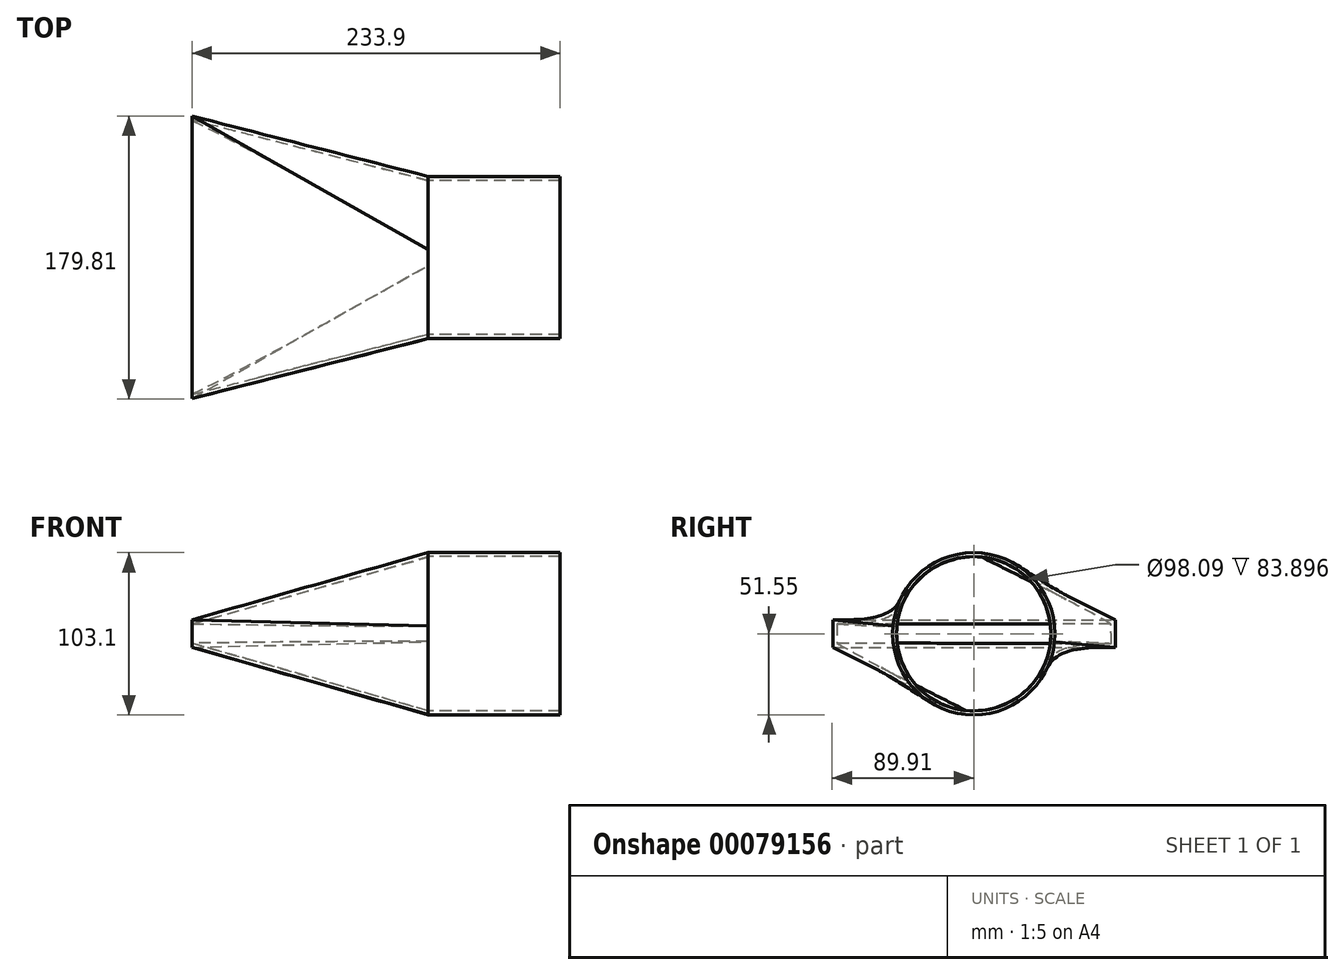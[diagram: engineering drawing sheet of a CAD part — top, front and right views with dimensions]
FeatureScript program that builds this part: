
annotation { "Feature Type Name" : "Feature", "Feature Type Description" : "" }
export const myFeature = defineFeature(function(context is Context, id is Id, definition is map)
    precondition{}
    {
        {
            var Q0;
            Q0=qCreatedBy(makeId("Right.planeOp"),FACE);
            cPlane(context, id + "F0", {"entities" : qUnion([Q0]), "cplaneType" : CPlaneType.OFFSET, "offset" : 150 * mm, "width" : 150 * mm, "height" : 150 * mm});
        }
        {
            var Q0;
            Q0=qCreatedBy(makeId("Right.planeOp"),FACE);
            var sketch = newSketch(context, id + "F1", { "sketchPlane" : qUnion([Q0])});
            skLineSegment(sketch, "E0.bottom", {"start": v(-89.53, 8.85) * mm, "end": v(89.9, 8.85) * mm});
            skLineSegment(sketch, "E0.top", {"start": v(-89.53, -8.57) * mm, "end": v(89.9, -8.57) * mm});
            skLineSegment(sketch, "E0.left", {"start": v(-89.53, 8.85) * mm, "end": v(-89.53, -8.57) * mm});
            skLineSegment(sketch, "E0.right", {"start": v(89.9, 8.85) * mm, "end": v(89.9, -8.57) * mm});
            skSolve(sketch);
        }
        {
            var Q0;
            Q0=qCreatedBy(id+"F0.planeOp",FACE);
            var sketch = newSketch(context, id + "F2", { "sketchPlane" : qUnion([Q0])});
            skCircle(sketch, "E1", {"center": v(0, 0) * mm, "radius": 51.55 * mm});
            skSolve(sketch);
        }
        {
            var Q0;
            Q0 = qSketchRegion(id + "F1", true);
            var Q1;
            Q1 = qSketchRegion(id + "F2", true);
            loft(context, id + "F3", {"sheetProfilesArray" : [{ "sheetProfileEntities" : qUnion([Q0]) }, { "sheetProfileEntities" : qUnion([Q1]) }]});
        }
        {
            var Q0;
            Q0=makeQuery(id+"F3.opLoft","CAP_FACE",FACE,{"disambiguationData":[OSD([makeQuery(id+"F2.imprint","IMPRINT",FACE,{"disambiguationData":[TD([[makeQuery(id+"F2.imprint","IMPRINT",EDGE,{"derivedFrom":sQuery(id+"F2.wireOp",EDGE,"E1")}),1.0]])]})])],"isStart":true});
            var Q1;
            Q1=makeQuery(id+"F3.opLoft","CAP_FACE",FACE,{"disambiguationData":[OSD([makeQuery(id+"F1.imprint","IMPRINT",FACE,{"disambiguationData":[TD([[makeQuery(id+"F1.imprint","IMPRINT",EDGE,{"derivedFrom":sQuery(id+"F1.wireOp",EDGE,"E0.bottom")}),-1.0]])]})])],"isStart":true});
            shell(context, id + "F4", {"entities" : qUnion([Q0, Q1]), "thickness" : 2.5 * mm});
        }
        {
            var Q0;
            Q0 = qSketchRegion(id + "F2", true);
            extrude(context, id + "F5", {"entities" : qUnion([Q0]), "depth" : 83.9 * mm});
        }
        {
            var Q0;
            Q0=makeQuery(id+"F5.opExtrude","CAP_FACE",FACE,{"disambiguationData":[OSD([sQuery(id+"F2.wireOp",EDGE,"E1")])],"isStart":false});
            var Q1;
            Q1=makeQuery(id+"F5.opExtrude","CAP_FACE",FACE,{"disambiguationData":[OSD([sQuery(id+"F2.wireOp",EDGE,"E1")])],"isStart":true});
            shell(context, id + "F6", {"entities" : qUnion([Q0, Q1]), "thickness" : 2.5 * mm});
        }
    });
